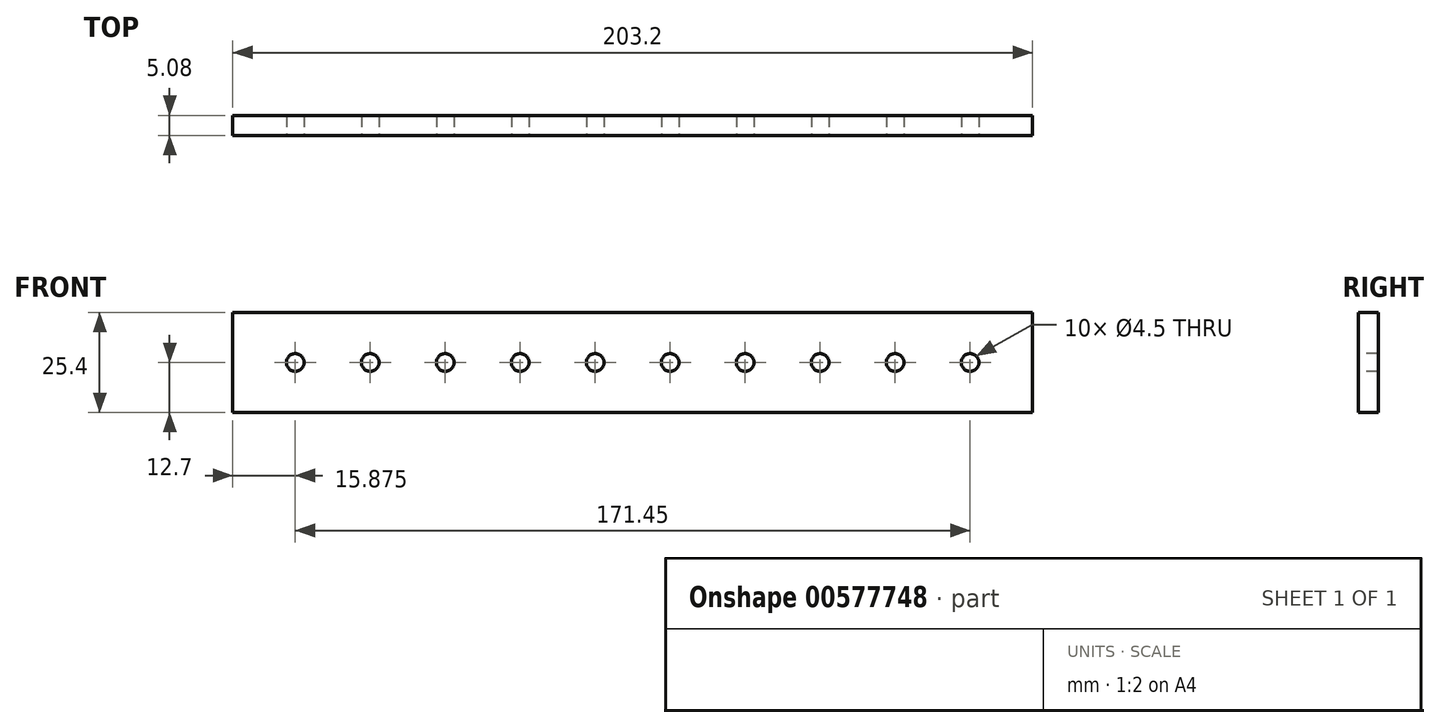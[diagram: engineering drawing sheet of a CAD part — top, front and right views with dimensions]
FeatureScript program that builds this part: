
annotation { "Feature Type Name" : "Feature", "Feature Type Description" : "" }
export const myFeature = defineFeature(function(context is Context, id is Id, definition is map)
    precondition{}
    {
        {
            var Q0;
            Q0=qCreatedBy(makeId("Front.planeOp"),FACE);
            var sketch = newSketch(context, id + "F0", { "sketchPlane" : qUnion([Q0])});
            skLineSegment(sketch, "E0.bottom", {"start": v(-101.6, 12.7) * mm, "end": v(101.6, 12.7) * mm});
            skLineSegment(sketch, "E0.top", {"start": v(-101.6, -12.7) * mm, "end": v(101.6, -12.7) * mm});
            skLineSegment(sketch, "E0.left", {"start": v(-101.6, 12.7) * mm, "end": v(-101.6, -12.7) * mm});
            skLineSegment(sketch, "E0.right", {"start": v(101.6, 12.7) * mm, "end": v(101.6, -12.7) * mm});
            skPoint(sketch, "E0.middle", {"position": v(0, 0) * mm});
            skLineSegment(sketch, "E1", {"start": v(-220.71, 0) * mm, "end": v(262.76, 0) * mm, "construction": true});
            skSolve(sketch);
        }
        {
            var Q0;
            Q0=qSketchRegion(id+"F0",true);
            extrude(context, id + "F1", {"entities" : qUnion([Q0]), "depth" : 5.08 * mm, "offsetDistance" : 25.4 * mm});
        }
        {
            var Q0;
            Q0=makeQuery(id+"F1.opExtrude","CAP_FACE",FACE,{"disambiguationData":[OSD([sQuery(id+"F0.wireOp",EDGE,"E0.bottom"),sQuery(id+"F0.wireOp",EDGE,"E0.top"),sQuery(id+"F0.wireOp",EDGE,"E0.left"),sQuery(id+"F0.wireOp",EDGE,"E0.right")])],"isStart":false});
            var sketch = newSketch(context, id + "F2", { "sketchPlane" : qUnion([Q0])});
            skLineSegment(sketch, "E2", {"start": v(-155.75, 0) * mm, "end": v(137.43, 0) * mm, "construction": true});
            skCircle(sketch, "E3", {"center": v(-85.73, 0) * mm, "radius": 2.25 * mm});
            skCircle(sketch, "E4.1.0.0", {"center": v(-66.68, 0) * mm, "radius": 2.25 * mm});
            skCircle(sketch, "E4.2.0.0", {"center": v(-47.63, 0) * mm, "radius": 2.25 * mm});
            skCircle(sketch, "E4.3.0.0", {"center": v(-28.58, 0) * mm, "radius": 2.25 * mm});
            skCircle(sketch, "E4.4.0.0", {"center": v(-9.53, 0) * mm, "radius": 2.25 * mm});
            skCircle(sketch, "E4.5.0.0", {"center": v(9.52, 0) * mm, "radius": 2.25 * mm});
            skCircle(sketch, "E4.6.0.0", {"center": v(28.57, 0) * mm, "radius": 2.25 * mm});
            skCircle(sketch, "E4.7.0.0", {"center": v(47.62, 0) * mm, "radius": 2.25 * mm});
            skCircle(sketch, "E4.8.0.0", {"center": v(66.67, 0) * mm, "radius": 2.25 * mm});
            skCircle(sketch, "E4.9.0.0", {"center": v(85.72, 0) * mm, "radius": 2.25 * mm});
            skLineSegment(sketch, "E4.direction1", {"start": v(-85.73, 0) * mm, "end": v(-66.68, 0) * mm, "construction": true});
            skSolve(sketch);
        }
        {
            var Q0;
            Q0=qSketchRegion(id+"F2",true);
            extrude(context, id + "F3", {"entities" : qUnion([Q0]), "operationType" : NewBodyOperationType.REMOVE, "oppositeDirection" : true, "depth" : 25.4 * mm, "offsetDistance" : 25.4 * mm});
        }
    });
